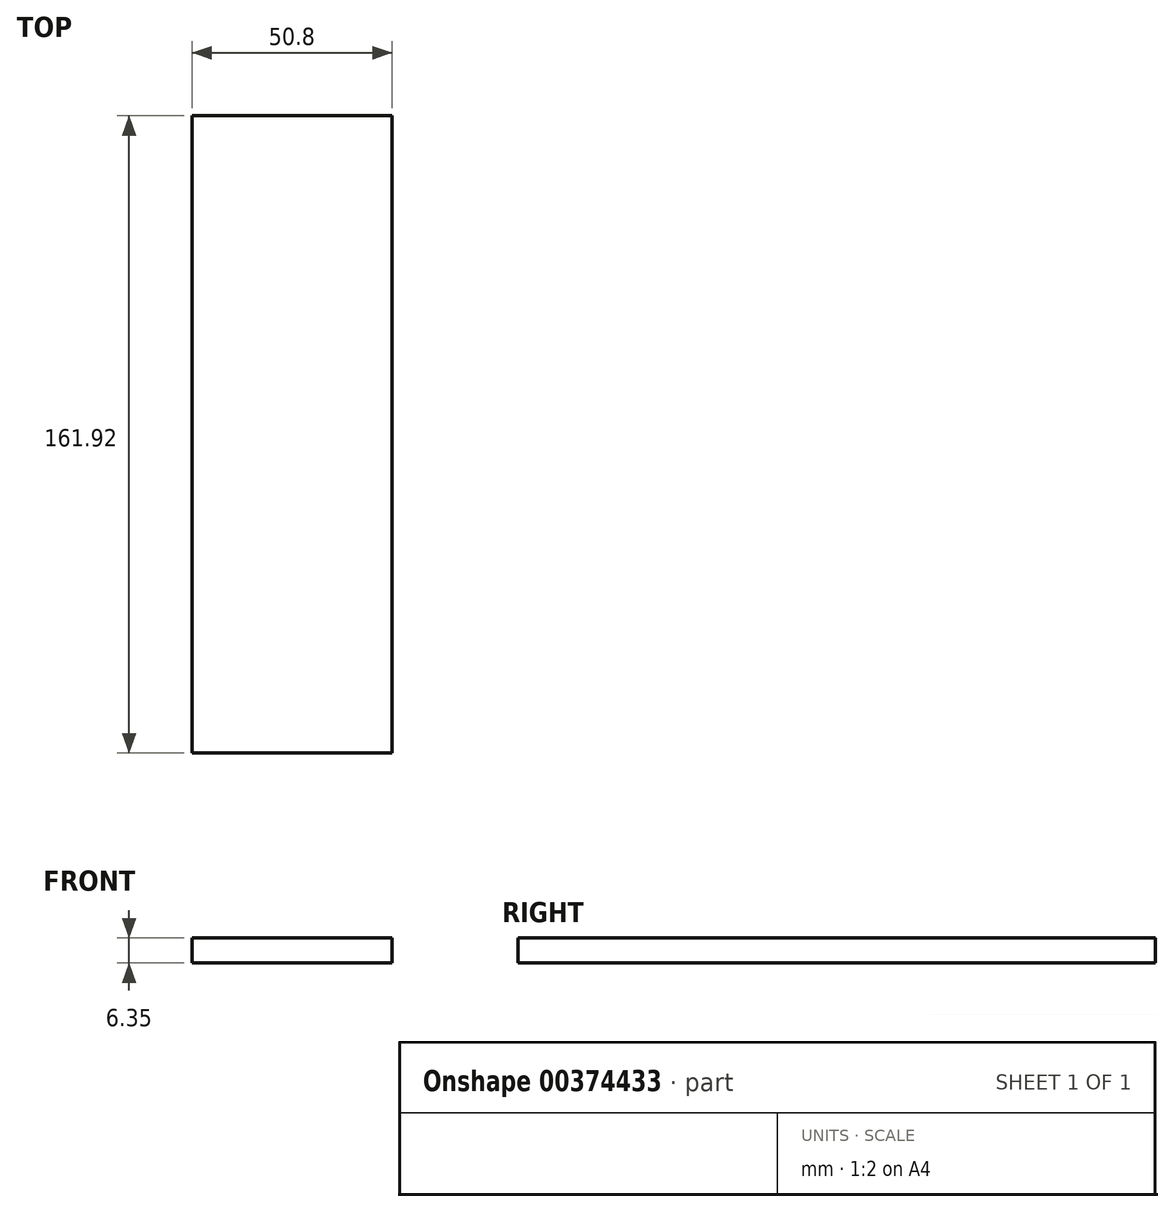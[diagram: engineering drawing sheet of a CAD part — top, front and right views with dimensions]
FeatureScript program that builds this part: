
annotation { "Feature Type Name" : "Feature", "Feature Type Description" : "" }
export const myFeature = defineFeature(function(context is Context, id is Id, definition is map)
    precondition{}
    {
        {
            var Q0;
            Q0=qCreatedBy(makeId("Front.planeOp"),FACE);
            var sketch = newSketch(context, id + "F0", { "sketchPlane" : qUnion([Q0])});
            skLineSegment(sketch, "E0.bottom", {"start": v(-23.84, -10.06) * mm, "end": v(26.96, -10.06) * mm});
            skLineSegment(sketch, "E0.top", {"start": v(-23.84, -3.7) * mm, "end": v(26.96, -3.7) * mm});
            skLineSegment(sketch, "E0.left", {"start": v(-23.84, -10.06) * mm, "end": v(-23.84, -3.7) * mm});
            skLineSegment(sketch, "E0.right", {"start": v(26.96, -10.06) * mm, "end": v(26.96, -3.7) * mm});
            skSolve(sketch);
        }
        {
            var Q0;
            Q0 = qSketchRegion(id + "F0", true);
            extrude(context, id + "F1", {"entities" : qUnion([Q0]), "endBound" : BoundingType.SYMMETRIC, "depth" : 161.92 * mm});
        }
    });
